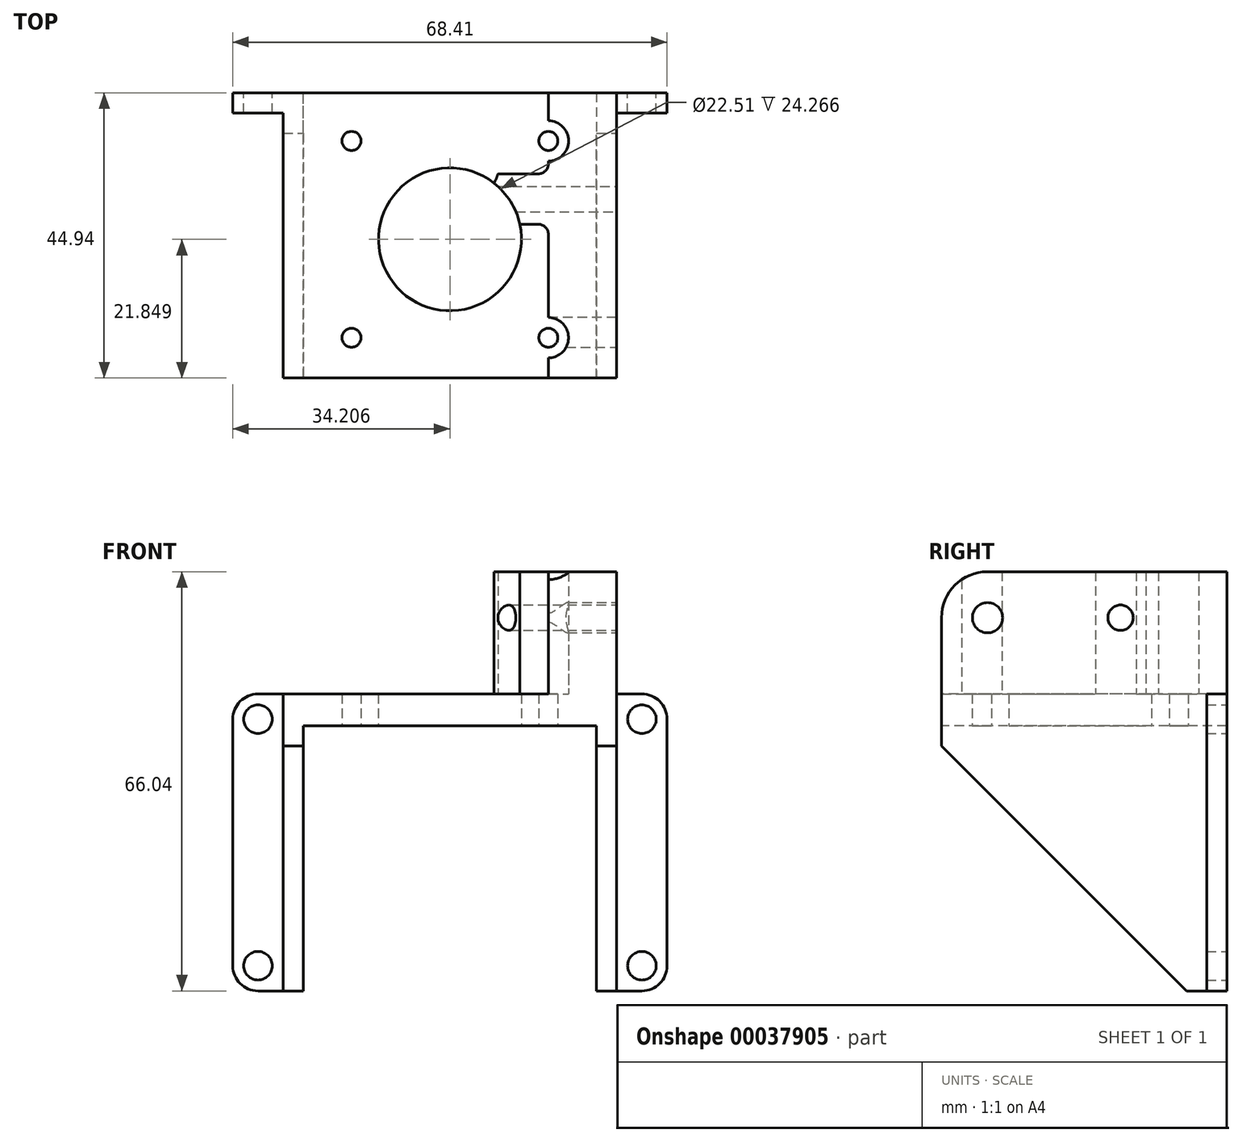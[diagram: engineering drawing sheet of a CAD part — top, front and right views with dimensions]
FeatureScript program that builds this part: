
annotation { "Feature Type Name" : "Feature", "Feature Type Description" : "" }
export const myFeature = defineFeature(function(context is Context, id is Id, definition is map)
    precondition{}
    {
        {
            var Q0;
            Q0=qCreatedBy(makeId("Top.planeOp"),FACE);
            var sketch = newSketch(context, id + "F0", { "sketchPlane" : qUnion([Q0])});
            skLineSegment(sketch, "E0.bottom", {"start": v(0, 0) * mm, "end": v(52.53, 0) * mm});
            skLineSegment(sketch, "E0.top", {"start": v(0, -44.94) * mm, "end": v(52.53, -44.94) * mm});
            skLineSegment(sketch, "E0.left", {"start": v(0, 0) * mm, "end": v(0, -44.94) * mm});
            skLineSegment(sketch, "E0.right", {"start": v(52.53, 0) * mm, "end": v(52.53, -44.94) * mm});
            skLineSegment(sketch, "E1.rect.bottom", {"start": v(41.77, -7.6) * mm, "end": v(10.77, -7.6) * mm, "construction": true});
            skLineSegment(sketch, "E1.rect.top", {"start": v(41.77, -38.6) * mm, "end": v(10.77, -38.6) * mm, "construction": true});
            skLineSegment(sketch, "E1.rect.left", {"start": v(41.77, -7.6) * mm, "end": v(41.77, -38.6) * mm, "construction": true});
            skLineSegment(sketch, "E1.rect.right", {"start": v(10.77, -7.6) * mm, "end": v(10.77, -38.6) * mm, "construction": true});
            skPoint(sketch, "E1.rect.middle", {"position": v(26.27, -23.1) * mm});
            skCircle(sketch, "E2", {"center": v(10.77, -7.6) * mm, "radius": 1.5 * mm});
            skCircle(sketch, "E3", {"center": v(26.27, -23.1) * mm, "radius": 11.25 * mm});
            skCircle(sketch, "E4", {"center": v(41.77, -7.6) * mm, "radius": 1.5 * mm});
            skCircle(sketch, "E5", {"center": v(41.77, -38.6) * mm, "radius": 1.5 * mm});
            skCircle(sketch, "E6", {"center": v(10.77, -38.6) * mm, "radius": 1.5 * mm});
            skLineSegment(sketch, "E7", {"start": v(26.27, -23.1) * mm, "end": v(26.27, 0) * mm, "construction": true});
            skCircle(sketch, "E8", {"center": v(10.77, -38.6) * mm, "radius": 6.35 * mm, "construction": true});
            skSolve(sketch);
        }
        {
            var Q0;
            Q0=qSketchRegion(id+"F0",true);
            extrude(context, id + "F1", {"entities" : qUnion([Q0]), "depth" : 5 * mm});
        }
        {
            var Q0;
            Q0=makeQuery(id+"F1.opExtrude","CAP_FACE",FACE,{"disambiguationData":[OSD([sQuery(id+"F0.wireOp",EDGE,"E0.bottom"),sQuery(id+"F0.wireOp",EDGE,"E0.top"),sQuery(id+"F0.wireOp",EDGE,"E0.left"),sQuery(id+"F0.wireOp",EDGE,"E0.right"),sQuery(id+"F0.wireOp",EDGE,"E2"),sQuery(id+"F0.wireOp",EDGE,"E3"),sQuery(id+"F0.wireOp",EDGE,"E4"),sQuery(id+"F0.wireOp",EDGE,"E5"),sQuery(id+"F0.wireOp",EDGE,"E6")])],"isStart":true});
            var sketch = newSketch(context, id + "F2", { "sketchPlane" : qUnion([Q0])});
            skLineSegment(sketch, "E9.bottom", {"start": v(0, 44.94) * mm, "end": v(3.18, 44.94) * mm});
            skLineSegment(sketch, "E9.top", {"start": v(0, 0) * mm, "end": v(3.18, 0) * mm});
            skLineSegment(sketch, "E9.left", {"start": v(0, 44.94) * mm, "end": v(0, 0) * mm});
            skLineSegment(sketch, "E9.right", {"start": v(3.18, 44.94) * mm, "end": v(3.18, 0) * mm});
            skLineSegment(sketch, "E10.bottom", {"start": v(52.53, 0) * mm, "end": v(49.36, 0) * mm});
            skLineSegment(sketch, "E10.top", {"start": v(52.53, 44.94) * mm, "end": v(49.36, 44.94) * mm});
            skLineSegment(sketch, "E10.left", {"start": v(52.53, 0) * mm, "end": v(52.53, 44.94) * mm});
            skLineSegment(sketch, "E10.right", {"start": v(49.36, 0) * mm, "end": v(49.36, 44.94) * mm});
            skSolve(sketch);
        }
        {
            var Q0;
            Q0 = qSketchRegion(id + "F2", true);
            extrude(context, id + "F3", {"entities" : qUnion([Q0]), "operationType" : NewBodyOperationType.ADD, "depth" : 41.77 * mm});
        }
        {
            var Q0;
            Q0=makeQuery(id+"F3.opExtrude","CAP_FACE",FACE,{"disambiguationData":[OSD([sQuery(id+"F2.wireOp",EDGE,"E9.bottom"),sQuery(id+"F2.wireOp",EDGE,"E9.top"),sQuery(id+"F2.wireOp",EDGE,"E9.left"),sQuery(id+"F2.wireOp",EDGE,"E9.right")])],"isStart":false});
            var sketch = newSketch(context, id + "F4", { "sketchPlane" : qUnion([Q0])});
            skLineSegment(sketch, "E11.bottom", {"start": v(0, 0) * mm, "end": v(-7.94, 0) * mm});
            skLineSegment(sketch, "E11.top", {"start": v(0, 3.18) * mm, "end": v(-7.94, 3.18) * mm});
            skLineSegment(sketch, "E11.left", {"start": v(0, 0) * mm, "end": v(0, 3.18) * mm});
            skLineSegment(sketch, "E11.right", {"start": v(-7.94, 0) * mm, "end": v(-7.94, 3.18) * mm});
            skLineSegment(sketch, "E12.bottom", {"start": v(52.53, 0) * mm, "end": v(60.47, 0) * mm});
            skLineSegment(sketch, "E12.top", {"start": v(52.53, 3.18) * mm, "end": v(60.47, 3.18) * mm});
            skLineSegment(sketch, "E12.left", {"start": v(52.53, 0) * mm, "end": v(52.53, 3.18) * mm});
            skLineSegment(sketch, "E12.right", {"start": v(60.47, 0) * mm, "end": v(60.47, 3.18) * mm});
            skSolve(sketch);
        }
        {
            var Q0;
            Q0 = qSketchRegion(id + "F4", true);
            var Q1;
            Q1=makeQuery(id+"F1.opExtrude","CAP_FACE",FACE,{"disambiguationData":[OSD([sQuery(id+"F0.wireOp",EDGE,"E0.bottom"),sQuery(id+"F0.wireOp",EDGE,"E0.top"),sQuery(id+"F0.wireOp",EDGE,"E0.left"),sQuery(id+"F0.wireOp",EDGE,"E0.right"),sQuery(id+"F0.wireOp",EDGE,"E2"),sQuery(id+"F0.wireOp",EDGE,"E3"),sQuery(id+"F0.wireOp",EDGE,"E4"),sQuery(id+"F0.wireOp",EDGE,"E5"),sQuery(id+"F0.wireOp",EDGE,"E6")])],"isStart":false});
            extrude(context, id + "F5", {"entities" : qUnion([Q0]), "operationType" : NewBodyOperationType.ADD, "endBound" : BoundingType.UP_TO_SURFACE, "oppositeDirection" : true, "endBoundEntityFace" : qUnion([Q1]), "depth" : 25.4 * mm});
        }
        {
            var Q0;
            Q0=makeQuery(id+"F5.opExtrude","CAP_EDGE",EDGE,{"disambiguationData":[OSD([sQuery(id+"F4.wireOp",EDGE,"E12.right")])],"isStart":true});
            var Q1;
            Q1=makeQuery(id+"F5.opExtrude","CAP_EDGE",EDGE,{"disambiguationData":[OSD([sQuery(id+"F4.wireOp",EDGE,"E12.right")])],"isStart":false});
            var Q2;
            Q2=makeQuery(id+"F5.opExtrude","CAP_EDGE",EDGE,{"disambiguationData":[OSD([sQuery(id+"F4.wireOp",EDGE,"E11.right")])],"isStart":false});
            var Q3;
            Q3=makeQuery(id+"F5.opExtrude","CAP_EDGE",EDGE,{"disambiguationData":[OSD([sQuery(id+"F4.wireOp",EDGE,"E11.right")])],"isStart":true});
            fillet(context, id + "F6", {"entities" : qUnion([Q0, Q1, Q2, Q3]), "radius" : 3.97 * mm, "tangentPropagation" : true, "allowEdgeOverflow" : false});
        }
        {
            var Q0;
            Q0=makeQuery(id+"F5.boolean.opBoolean","MERGE",FACE,{"derivedFrom":[makeQuery(id+"F3.boolean.opBoolean","MERGE",FACE,{"derivedFrom":[makeQuery(id+"F1.opExtrude","SWEPT_FACE",FACE,{"disambiguationData":[OSD([sQuery(id+"F0.wireOp",EDGE,"E0.bottom")])]}),makeQuery(id+"F3.opExtrude","SWEPT_FACE",FACE,{"disambiguationData":[OSD([sQuery(id+"F2.wireOp",EDGE,"E9.top")])]}),makeQuery(id+"F3.opExtrude","SWEPT_FACE",FACE,{"disambiguationData":[OSD([sQuery(id+"F2.wireOp",EDGE,"E10.bottom")])]})]}),makeQuery(id+"F5.opExtrude","SWEPT_FACE",FACE,{"disambiguationData":[OSD([sQuery(id+"F4.wireOp",EDGE,"E11.bottom")])]}),makeQuery(id+"F5.opExtrude","SWEPT_FACE",FACE,{"disambiguationData":[OSD([sQuery(id+"F4.wireOp",EDGE,"E12.bottom")])]})]});
            var sketch = newSketch(context, id + "F7", { "sketchPlane" : qUnion([Q0])});
            skCircle(sketch, "E13", {"center": v(3.97, -37.8) * mm, "radius": 2.25 * mm});
            skCircle(sketch, "E14", {"center": v(3.97, 1.03) * mm, "radius": 2.25 * mm});
            skCircle(sketch, "E15", {"center": v(-56.5, 1.03) * mm, "radius": 2.25 * mm});
            skCircle(sketch, "E16", {"center": v(-56.5, -37.8) * mm, "radius": 2.25 * mm});
            skSolve(sketch);
        }
        {
            var Q0;
            Q0 = qSketchRegion(id + "F7", true);
            var Q1;
            Q1=makeQuery(id+"F5.opExtrude","SWEPT_FACE",FACE,{"disambiguationData":[OSD([sQuery(id+"F4.wireOp",EDGE,"E12.top")])]});
            extrude(context, id + "F8", {"entities" : qUnion([Q0]), "operationType" : NewBodyOperationType.REMOVE, "endBound" : BoundingType.UP_TO_SURFACE, "oppositeDirection" : true, "endBoundEntityFace" : qUnion([Q1]), "depth" : 25.4 * mm});
        }
        {
            var Q0;
            Q0=makeQuery(id+"F3.boolean.opBoolean","MERGE",FACE,{"derivedFrom":[makeQuery(id+"F1.opExtrude","SWEPT_FACE",FACE,{"disambiguationData":[OSD([sQuery(id+"F0.wireOp",EDGE,"E0.right")])]}),makeQuery(id+"F3.opExtrude","SWEPT_FACE",FACE,{"disambiguationData":[OSD([sQuery(id+"F2.wireOp",EDGE,"E10.left")])]})]});
            var sketch = newSketch(context, id + "F9", { "sketchPlane" : qUnion([Q0])});
            skLineSegment(sketch, "E17.top", {"start": v(-44.94, -41.77) * mm, "end": v(-6.35, -41.77) * mm});
            skLineSegment(sketch, "E17.left", {"start": v(-44.94, -3.18) * mm, "end": v(-44.94, -41.77) * mm});
            skLineSegment(sketch, "E18", {"start": v(-44.94, -3.18) * mm, "end": v(-44.94, 0) * mm, "construction": true});
            skLineSegment(sketch, "E19", {"start": v(-6.35, -41.77) * mm, "end": v(-3.18, -41.77) * mm, "construction": true});
            skLineSegment(sketch, "E20", {"start": v(-6.35, -41.77) * mm, "end": v(-44.94, -3.17) * mm});
            skSolve(sketch);
        }
        {
            var Q0;
            Q0 = qSketchRegion(id + "F9", true);
            var Q1;
            Q1=makeQuery(id+"F3.boolean.opBoolean","MERGE",FACE,{"derivedFrom":[makeQuery(id+"F1.opExtrude","SWEPT_FACE",FACE,{"disambiguationData":[OSD([sQuery(id+"F0.wireOp",EDGE,"E0.left")])]}),makeQuery(id+"F3.opExtrude","SWEPT_FACE",FACE,{"disambiguationData":[OSD([sQuery(id+"F2.wireOp",EDGE,"E9.left")])]})]});
            extrude(context, id + "F10", {"entities" : qUnion([Q0]), "operationType" : NewBodyOperationType.REMOVE, "endBound" : BoundingType.UP_TO_SURFACE, "oppositeDirection" : true, "endBoundEntityFace" : qUnion([Q1]), "depth" : 25.4 * mm});
        }
        {
            var Q0;
            Q0=makeQuery(id+"F5.boolean.opBoolean","MERGE",FACE,{"derivedFrom":[makeQuery(id+"F1.opExtrude","CAP_FACE",FACE,{"disambiguationData":[OSD([sQuery(id+"F0.wireOp",EDGE,"E0.bottom"),sQuery(id+"F0.wireOp",EDGE,"E0.top"),sQuery(id+"F0.wireOp",EDGE,"E0.left"),sQuery(id+"F0.wireOp",EDGE,"E0.right"),sQuery(id+"F0.wireOp",EDGE,"E2"),sQuery(id+"F0.wireOp",EDGE,"E3"),sQuery(id+"F0.wireOp",EDGE,"E4"),sQuery(id+"F0.wireOp",EDGE,"E5"),sQuery(id+"F0.wireOp",EDGE,"E6")])],"isStart":false}),makeQuery(id+"F5.opExtrude","CAP_FACE",FACE,{"disambiguationData":[OSD([sQuery(id+"F4.wireOp",EDGE,"E11.bottom"),sQuery(id+"F4.wireOp",EDGE,"E11.top"),sQuery(id+"F4.wireOp",EDGE,"E11.left"),sQuery(id+"F4.wireOp",EDGE,"E11.right")])],"isStart":false}),makeQuery(id+"F5.opExtrude","CAP_FACE",FACE,{"disambiguationData":[OSD([sQuery(id+"F4.wireOp",EDGE,"E12.bottom"),sQuery(id+"F4.wireOp",EDGE,"E12.top"),sQuery(id+"F4.wireOp",EDGE,"E12.left"),sQuery(id+"F4.wireOp",EDGE,"E12.right")])],"isStart":false})]});
            var sketch = newSketch(context, id + "F11", { "sketchPlane" : qUnion([Q0])});
            skLineSegment(sketch, "E21.bottom", {"start": v(52.53, -44.94) * mm, "end": v(41.77, -44.94) * mm});
            skLineSegment(sketch, "E21.top", {"start": v(52.53, -30.44) * mm, "end": v(41.77, -30.44) * mm});
            skLineSegment(sketch, "E21.left", {"start": v(52.53, -44.94) * mm, "end": v(52.53, -30.44) * mm});
            skArc(sketch, "E22", {"start": v(41.77, -41.77) * mm, "mid": v(44.94, -38.6) * mm, "end": v(41.77, -35.42) * mm});
            skLineSegment(sketch, "E23", {"start": v(41.77, -44.94) * mm, "end": v(41.77, -41.77) * mm});
            skLineSegment(sketch, "E24", {"start": v(41.77, -41.77) * mm, "end": v(41.77, -35.42) * mm, "construction": true});
            skLineSegment(sketch, "E25", {"start": v(41.77, -35.42) * mm, "end": v(41.77, -30.44) * mm});
            skLineSegment(sketch, "E26", {"start": v(26.27, -23.1) * mm, "end": v(26.27, -16.74) * mm, "construction": true});
            skLineSegment(sketch, "E27.top", {"start": v(52.53, -12.77) * mm, "end": v(30.75, -12.77) * mm});
            skLineSegment(sketch, "E27.left", {"start": v(52.53, -20.7) * mm, "end": v(52.53, -12.77) * mm});
            skLineSegment(sketch, "E27.right", {"start": v(30.75, -20.7) * mm, "end": v(30.75, -12.77) * mm});
            skLineSegment(sketch, "E28", {"start": v(26.27, -16.74) * mm, "end": v(30.75, -16.74) * mm, "construction": true});
            skLineSegment(sketch, "E29", {"start": v(52.53, -20.7) * mm, "end": v(37.26, -20.7) * mm});
            skLineSegment(sketch, "E30", {"start": v(37.26, -20.7) * mm, "end": v(30.75, -20.7) * mm, "construction": true});
            skArc(sketch, "E31", {"start": v(37.26, -20.7) * mm, "mid": v(34.97, -15.96) * mm, "end": v(30.75, -12.77) * mm});
            skSolve(sketch);
        }
        {
            var Q0;
            Q0 = qSketchRegion(id + "F11", true);
            var Q1;
            {var subQ2=sQuery(id+"F11.wireOp",EDGE,"330cf8d8-da5a-4c49-9072-953a09258db2.bottom");Q1=makeQuery(id+"F11.imprint","IMPRINT",FACE,{"disambiguationData":[TD([[makeQuery(id+"F11.imprint","IMPRINT",EDGE,{"derivedFrom":subQ2}),1.0]])]});}
            extrude(context, id + "F12", {"entities" : qUnion([Q0, Q1]), "operationType" : NewBodyOperationType.ADD, "depth" : 19.27 * mm});
        }
        {
            var Q0;
            Q0=makeQuery(id+"F12.boolean.opBoolean","MERGE",FACE,{"derivedFrom":[makeQuery(id+"F3.boolean.opBoolean","MERGE",FACE,{"derivedFrom":[makeQuery(id+"F1.opExtrude","SWEPT_FACE",FACE,{"disambiguationData":[OSD([sQuery(id+"F0.wireOp",EDGE,"E0.right")])]}),makeQuery(id+"F3.opExtrude","SWEPT_FACE",FACE,{"disambiguationData":[OSD([sQuery(id+"F2.wireOp",EDGE,"E10.left")])]})]}),makeQuery(id+"F12.opExtrude","SWEPT_FACE",FACE,{"disambiguationData":[OSD([sQuery(id+"F11.wireOp",EDGE,"E21.left")])]})]});
            var sketch = newSketch(context, id + "F13", { "sketchPlane" : qUnion([Q0])});
            skLineSegment(sketch, "E32", {"start": v(-37.69, 17.01) * mm, "end": v(-37.69, 5) * mm});
            skLineSegment(sketch, "E33", {"start": v(-30.44, 5) * mm, "end": v(-37.69, 5) * mm});
            skLineSegment(sketch, "E34", {"start": v(-37.69, 17.01) * mm, "end": v(-44.94, 17.01) * mm});
            skCircle(sketch, "E35", {"center": v(-37.69, 17.01) * mm, "radius": 2.38 * mm});
            skSolve(sketch);
        }
        {
            var Q0;
            Q0 = qSketchRegion(id + "F13", true);
            var Q1;
            Q1=makeQuery(id+"F12.opExtrude","SWEPT_FACE",FACE,{"disambiguationData":[OSD([sQuery(id+"F11.wireOp",EDGE,"E25")])]});
            extrude(context, id + "F14", {"entities" : qUnion([Q0]), "operationType" : NewBodyOperationType.REMOVE, "endBound" : BoundingType.UP_TO_SURFACE, "oppositeDirection" : true, "endBoundEntityFace" : qUnion([Q1]), "depth" : 25.4 * mm});
        }
        {
            var Q0;
            Q0=makeQuery(id+"F5.boolean.opBoolean","MERGE",FACE,{"derivedFrom":[makeQuery(id+"F1.opExtrude","CAP_FACE",FACE,{"disambiguationData":[OSD([sQuery(id+"F0.wireOp",EDGE,"E0.bottom"),sQuery(id+"F0.wireOp",EDGE,"E0.top"),sQuery(id+"F0.wireOp",EDGE,"E0.left"),sQuery(id+"F0.wireOp",EDGE,"E0.right"),sQuery(id+"F0.wireOp",EDGE,"E2"),sQuery(id+"F0.wireOp",EDGE,"E3"),sQuery(id+"F0.wireOp",EDGE,"E4"),sQuery(id+"F0.wireOp",EDGE,"E5"),sQuery(id+"F0.wireOp",EDGE,"E6")])],"isStart":false}),makeQuery(id+"F5.opExtrude","CAP_FACE",FACE,{"disambiguationData":[OSD([sQuery(id+"F4.wireOp",EDGE,"E11.bottom"),sQuery(id+"F4.wireOp",EDGE,"E11.top"),sQuery(id+"F4.wireOp",EDGE,"E11.left"),sQuery(id+"F4.wireOp",EDGE,"E11.right")])],"isStart":false}),makeQuery(id+"F5.opExtrude","CAP_FACE",FACE,{"disambiguationData":[OSD([sQuery(id+"F4.wireOp",EDGE,"E12.bottom"),sQuery(id+"F4.wireOp",EDGE,"E12.top"),sQuery(id+"F4.wireOp",EDGE,"E12.left"),sQuery(id+"F4.wireOp",EDGE,"E12.right")])],"isStart":false})]});
            var sketch = newSketch(context, id + "F15", { "sketchPlane" : qUnion([Q0])});
            skCircle(sketch, "E36", {"center": v(26.27, -23.1) * mm, "radius": 6.35 * mm, "construction": true});
            skCircle(sketch, "E37", {"center": v(26.27, -10.4) * mm, "radius": 6.35 * mm, "construction": true});
            skLineSegment(sketch, "E38", {"start": v(26.27, -23.1) * mm, "end": v(26.27, -10.4) * mm, "construction": true});
            skCircle(sketch, "E39", {"center": v(26.27, -10.4) * mm, "radius": 7.94 * mm});
            skSolve(sketch);
        }
        {
            var Q0;
            Q0 = qSketchRegion(id + "F15", true);
            extrude(context, id + "F16", {"entities" : qUnion([Q0]), "operationType" : NewBodyOperationType.REMOVE, "depth" : 25.4 * mm});
        }
        {
            var Q0;
            Q0=makeQuery(id+"F12.opExtrude","SWEPT_FACE",FACE,{"disambiguationData":[OSD([sQuery(id+"F11.wireOp",EDGE,"E21.top")])]});
            var Q1;
            Q1=makeQuery(id+"F5.boolean.opBoolean","MERGE",FACE,{"derivedFrom":[makeQuery(id+"F3.boolean.opBoolean","MERGE",FACE,{"derivedFrom":[makeQuery(id+"F1.opExtrude","SWEPT_FACE",FACE,{"disambiguationData":[OSD([sQuery(id+"F0.wireOp",EDGE,"E0.bottom")])]}),makeQuery(id+"F3.opExtrude","SWEPT_FACE",FACE,{"disambiguationData":[OSD([sQuery(id+"F2.wireOp",EDGE,"E9.top")])]}),makeQuery(id+"F3.opExtrude","SWEPT_FACE",FACE,{"disambiguationData":[OSD([sQuery(id+"F2.wireOp",EDGE,"E10.bottom")])]})]}),makeQuery(id+"F5.opExtrude","SWEPT_FACE",FACE,{"disambiguationData":[OSD([sQuery(id+"F4.wireOp",EDGE,"E11.bottom")])]}),makeQuery(id+"F5.opExtrude","SWEPT_FACE",FACE,{"disambiguationData":[OSD([sQuery(id+"F4.wireOp",EDGE,"E12.bottom")])]})]});
            extrude(context, id + "F17", {"entities" : qUnion([Q0]), "operationType" : NewBodyOperationType.ADD, "endBound" : BoundingType.UP_TO_SURFACE, "endBoundEntityFace" : qUnion([Q1]), "depth" : 25.4 * mm});
        }
        {
            var Q0;
            {var subQ0=sQuery(id+"F0.wireOp",EDGE,"E0.bottom");var subQ1=sQuery(id+"F0.wireOp",EDGE,"E0.top");var subQ2=sQuery(id+"F0.wireOp",EDGE,"E0.left");var subQ3=sQuery(id+"F0.wireOp",EDGE,"E2");var subQ4=sQuery(id+"F0.wireOp",EDGE,"E3");var subQ5=sQuery(id+"F0.wireOp",EDGE,"E4");var subQ6=sQuery(id+"F0.wireOp",EDGE,"E5");var subQ7=sQuery(id+"F0.wireOp",EDGE,"E6");var subQ8=sQuery(id+"F4.wireOp",EDGE,"E11.bottom");var subQ9=sQuery(id+"F4.wireOp",EDGE,"E11.top");var subQ10=sQuery(id+"F4.wireOp",EDGE,"E11.right");var subQ11=sQuery(id+"F4.wireOp",EDGE,"E12.bottom");var subQ12=sQuery(id+"F15.wireOp",EDGE,"E39");Q0=makeQuery(id+"F17.boolean.opBoolean","SPLIT",FACE,{"disambiguationData":[TD([makeQuery(id+"F1.opExtrude","SWEPT_FACE",FACE,{"disambiguationData":[OSD([subQ1])]})])],"derivedFrom":makeQuery(id+"F16.boolean.opBoolean","MERGE",FACE,{"derivedFrom":[makeQuery(id+"F5.boolean.opBoolean","MERGE",FACE,{"derivedFrom":[makeQuery(id+"F1.opExtrude","CAP_FACE",FACE,{"disambiguationData":[OSD([subQ0,subQ1,subQ2,sQuery(id+"F0.wireOp",EDGE,"E0.right"),subQ3,subQ4,subQ5,subQ6,subQ7])],"isStart":false}),makeQuery(id+"F5.opExtrude","CAP_FACE",FACE,{"disambiguationData":[OSD([subQ8,subQ9,sQuery(id+"F4.wireOp",EDGE,"E11.left"),subQ10])],"isStart":false}),makeQuery(id+"F5.opExtrude","CAP_FACE",FACE,{"disambiguationData":[OSD([subQ11,sQuery(id+"F4.wireOp",EDGE,"E12.top"),sQuery(id+"F4.wireOp",EDGE,"E12.left"),sQuery(id+"F4.wireOp",EDGE,"E12.right")])],"isStart":false})]}),makeQuery(id+"F16.opExtrude","CAP_FACE",FACE,{"disambiguationData":[OSD([subQ12])],"isStart":true})]})});}
            var sketch = newSketch(context, id + "F18", { "sketchPlane" : qUnion([Q0])});
            skCircle(sketch, "E40", {"center": v(41.77, -7.6) * mm, "radius": 3.18 * mm});
            skSolve(sketch);
        }
        {
            var Q0;
            Q0 = qSketchRegion(id + "F18", true);
            var Q1;
            {var subQ0=sQuery(id+"F11.wireOp",EDGE,"E21.top");Q1=makeQuery(id+"F17.boolean.opBoolean","MERGE",FACE,{"derivedFrom":[makeQuery(id+"F12.opExtrude","CAP_FACE",FACE,{"disambiguationData":[OSD([sQuery(id+"F11.wireOp",EDGE,"E21.bottom"),subQ0,sQuery(id+"F11.wireOp",EDGE,"E21.left"),sQuery(id+"F11.wireOp",EDGE,"E22"),sQuery(id+"F11.wireOp",EDGE,"E23"),sQuery(id+"F11.wireOp",EDGE,"E25")])],"isStart":false}),makeQuery(id+"F12.opExtrude","CAP_FACE",FACE,{"disambiguationData":[OSD([sQuery(id+"F11.wireOp",EDGE,"E27.top"),sQuery(id+"F11.wireOp",EDGE,"E27.left"),sQuery(id+"F11.wireOp",EDGE,"E29"),sQuery(id+"F11.wireOp",EDGE,"E31")])],"isStart":false}),makeQuery(id+"F17.opExtrude","SWEPT_FACE",FACE,{"disambiguationData":[OSD([subQ0]),TDD([makeQuery(id+"F12.opExtrude","CAP_EDGE",EDGE,{"disambiguationData":[OSD([subQ0])],"isStart":false})])]})]});}
            extrude(context, id + "F19", {"entities" : qUnion([Q0]), "operationType" : NewBodyOperationType.REMOVE, "endBound" : BoundingType.UP_TO_SURFACE, "endBoundEntityFace" : qUnion([Q1]), "depth" : 25.4 * mm});
        }
        {
            var Q0;
            {var subQ0=sQuery(id+"F0.wireOp",EDGE,"E0.right");var subQ1=sQuery(id+"F11.wireOp",EDGE,"E21.left");Q0=makeQuery(id+"F17.boolean.opBoolean","MERGE",FACE,{"derivedFrom":[makeQuery(id+"F12.boolean.opBoolean","MERGE",FACE,{"derivedFrom":[makeQuery(id+"F3.boolean.opBoolean","MERGE",FACE,{"derivedFrom":[makeQuery(id+"F1.opExtrude","SWEPT_FACE",FACE,{"disambiguationData":[OSD([subQ0])]}),makeQuery(id+"F3.opExtrude","SWEPT_FACE",FACE,{"disambiguationData":[OSD([sQuery(id+"F2.wireOp",EDGE,"E10.left")])]})]}),makeQuery(id+"F12.opExtrude","SWEPT_FACE",FACE,{"disambiguationData":[OSD([subQ1])]}),makeQuery(id+"F12.opExtrude","SWEPT_FACE",FACE,{"disambiguationData":[OSD([sQuery(id+"F11.wireOp",EDGE,"E27.left")])]})]}),makeQuery(id+"F17.opExtrude","SWEPT_FACE",FACE,{"disambiguationData":[OSD([subQ0,sQuery(id+"F11.wireOp",EDGE,"E21.top"),subQ1])]})]});}
            var sketch = newSketch(context, id + "F20", { "sketchPlane" : qUnion([Q0])});
            skLineSegment(sketch, "E41", {"start": v(-37.69, 17.01) * mm, "end": v(-16.74, 17.01) * mm});
            skCircle(sketch, "E42", {"center": v(-16.74, 17.01) * mm, "radius": 2 * mm});
            skLineSegment(sketch, "E43", {"start": v(-16.74, 17.01) * mm, "end": v(-16.74, 24.27) * mm});
            skLineSegment(sketch, "E44", {"start": v(-20.7, 24.27) * mm, "end": v(-12.77, 24.27) * mm});
            skSolve(sketch);
        }
        {
            var Q0;
            Q0 = qSketchRegion(id + "F20", true);
            var Q1;
            Q1=makeQuery(id+"F12.boolean.opBoolean","MERGE",FACE,{"derivedFrom":[makeQuery(id+"F1.opExtrude","SWEPT_FACE",FACE,{"disambiguationData":[OSD([sQuery(id+"F0.wireOp",EDGE,"E3")])]}),makeQuery(id+"F12.opExtrude","SWEPT_FACE",FACE,{"disambiguationData":[OSD([sQuery(id+"F11.wireOp",EDGE,"E31")])]})]});
            extrude(context, id + "F21", {"entities" : qUnion([Q0]), "operationType" : NewBodyOperationType.REMOVE, "endBound" : BoundingType.UP_TO_SURFACE, "oppositeDirection" : true, "endBoundEntityFace" : qUnion([Q1]), "depth" : 25.4 * mm});
        }
        {
            var Q0;
            Q0=makeQuery(id+"F12.opExtrude","CAP_EDGE",EDGE,{"disambiguationData":[OSD([sQuery(id+"F11.wireOp",EDGE,"E21.bottom")])],"isStart":false});
            fillet(context, id + "F22", {"entities" : qUnion([Q0]), "radius" : 7.25 * mm, "tangentPropagation" : true, "allowEdgeOverflow" : false});
        }
        {
            var Q0;
            Q0=makeQuery(id+"F17.boolean.opBoolean","INTERSECT",EDGE,{"derivedFrom":[makeQuery(id+"F12.opExtrude","SWEPT_FACE",FACE,{"disambiguationData":[OSD([sQuery(id+"F11.wireOp",EDGE,"E29")])]}),makeQuery(id+"F17.opExtrude","SWEPT_FACE",FACE,{"disambiguationData":[OSD([sQuery(id+"F11.wireOp",EDGE,"E21.top"),sQuery(id+"F11.wireOp",EDGE,"E25")])]})]});
            var Q1;
            Q1=makeQuery(id+"F17.boolean.opBoolean","INTERSECT",EDGE,{"derivedFrom":[makeQuery(id+"F12.opExtrude","SWEPT_FACE",FACE,{"disambiguationData":[OSD([sQuery(id+"F11.wireOp",EDGE,"E27.top")])]}),makeQuery(id+"F17.opExtrude","SWEPT_FACE",FACE,{"disambiguationData":[OSD([sQuery(id+"F11.wireOp",EDGE,"E21.top"),sQuery(id+"F11.wireOp",EDGE,"E25")])]})]});
            fillet(context, id + "F23", {"entities" : qUnion([Q0, Q1]), "radius" : 1.59 * mm, "tangentPropagation" : true, "allowEdgeOverflow" : false});
        }
    });
